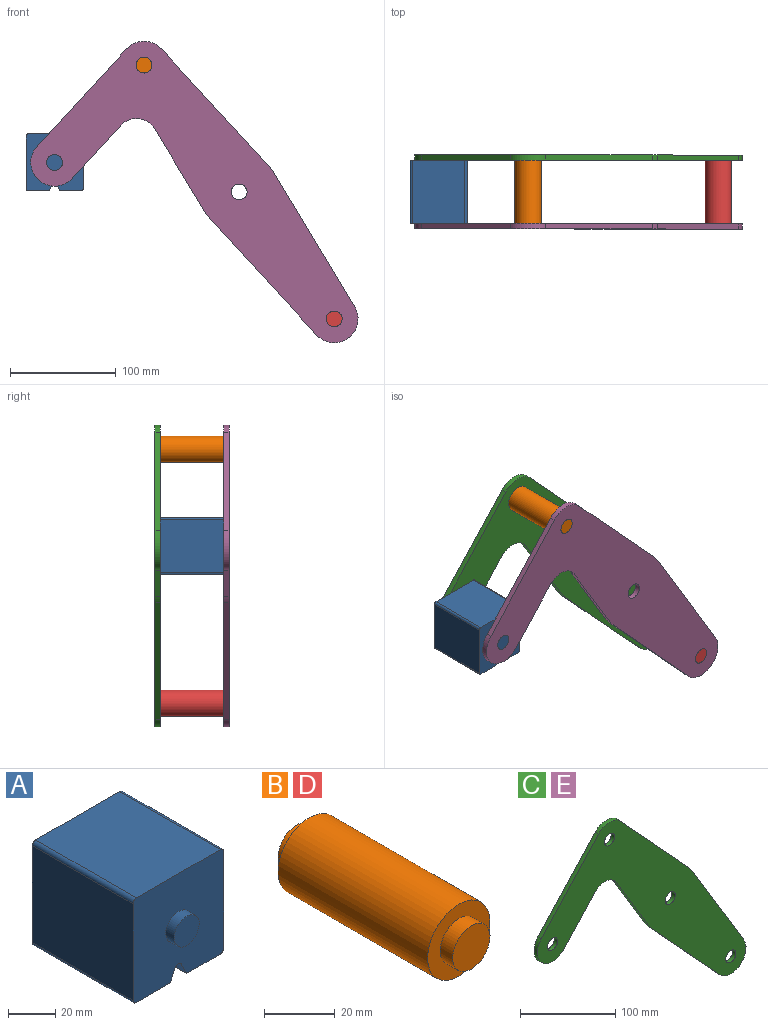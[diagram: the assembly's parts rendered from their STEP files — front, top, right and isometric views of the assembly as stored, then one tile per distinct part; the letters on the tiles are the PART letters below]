
ASSEMBLY  parts=5 mates=3
PART A: 18 faces, bbox 54x70x54 mm
  f0: plane 60x50.01mm, normal (0,0,1), area 3000.4mm2, adj f4,f10,f13,f14
  f1: plane 60x50.01mm, normal (-1,0,0), area 3000.4mm2, adj f4,f10,f14,f15
  f2: plane 60x20mm, normal (0,0,-1), area 1200.2mm2, adj f3,f4,f10,f15
  f3: plane 60x6.42mm, normal (0.89,0,-0.45), area 430.8mm2, adj f2,f4,f10,f16
  f4: plane 54.01x54.01mm, normal (0,-1,0), area 2690.1mm2, adj f0,f1,f2,f3,f5,f6,f7,f9
  f5: plane 60x50.01mm, normal (1,0,0), area 3000.4mm2, adj f4,f10,f13,f17
  f6: plane 60x6.42mm, normal (-0.89,0,-0.45), area 430.8mm2, adj f4,f7,f10,f16
  f7: plane 60x20mm, normal (0,0,-1), area 1200.2mm2, adj f4,f6,f10,f17
  f8: plane 15x15mm, normal (0,-1,0), area 176.7mm2, adj f9
  f9: cylinder r=7.5mm len=15mm, axis (0,1,0), area 235.6mm2, adj f4,f8
  f10: plane 54.01x54.01mm, normal (0,1,0), area 2690.1mm2, adj f0,f1,f2,f3,f5,f6,f7,f12
  f11: plane 15x15mm, normal (0,1,0), area 176.7mm2, adj f12
  f12: cylinder r=7.5mm len=15mm, axis (0,-1,0), area 235.6mm2, adj f10,f11
  f13: cylinder r=2mm len=60mm, axis (0,-1,0), area 188.5mm2, adj f0,f4,f5,f10
  f14: cylinder r=2mm len=60mm, axis (0,1,0), area 188.5mm2, adj f0,f1,f4,f10
  f15: cylinder r=2mm len=60mm, axis (0,-1,0), area 188.5mm2, adj f1,f2,f4,f10
  f16: cylinder r=2mm len=60mm, axis (0,-1,0), area 265.7mm2, adj f3,f4,f6,f10
  f17: cylinder r=2mm len=60mm, axis (0,1,0), area 188.5mm2, adj f4,f5,f7,f10
PART B: 7 faces, bbox 25x70x25 mm
  f0: cylinder r=12.5mm len=60mm, axis (0,-1,0), area 4712.4mm2, adj f2,f5
  f1: cylinder r=7.5mm len=15mm, axis (0,1,0), area 235.6mm2, adj f2,f3
  f2: plane 25x25mm, normal (0,-1,0), area 314.2mm2, adj f0,f1
  f3: plane 15x15mm, normal (0,-1,0), area 176.7mm2, adj f1
  f4: cylinder r=7.5mm len=15mm, axis (0,-1,0), area 235.6mm2, adj f5,f6
  f5: plane 25x25mm, normal (0,1,0), area 314.2mm2, adj f0,f4
  f6: plane 15x15mm, normal (0,1,0), area 176.7mm2, adj f4
PART C: 18 faces, bbox 309.5x5x285.1 mm
  f0: cylinder r=22.5mm len=39.07mm, axis (0,1,0), area 353.4mm2, adj f1,f13,f16,f17
  f1: plane 50.28x46.21mm, normal (0.74,0,-0.68), area 341.4mm2, adj f0,f2,f16,f17
  f2: cylinder r=20mm len=31.85mm, axis (0,1,0), area 185.5mm2, adj f1,f3,f16,f17
  f3: plane 79.23x47.81mm, normal (-0.86,0,-0.52), area 462.7mm2, adj f2,f4,f16,f17
  f4: cylinder r=37.5mm len=6mm, axis (0,1,0), area 37.6mm2, adj f3,f5,f16,f17
  f5: plane 109.88x101mm, normal (-0.74,0,-0.68), area 746.2mm2, adj f4,f6,f16,f17
  f6: cylinder r=22.5mm len=39.07mm, axis (0,1,0), area 330.9mm2, adj f5,f7,f16,f17
  f7: plane 127.78x77.11mm, normal (0.86,0,0.52), area 746.2mm2, adj f6,f8,f16,f17
  f8: cylinder r=37.5mm len=6mm, axis (0,1,0), area 37.6mm2, adj f7,f9,f16,f17
  f9: plane 109.88x101mm, normal (0.74,0,0.68), area 746.2mm2, adj f8,f10,f16,f17
  f10: cylinder r=22.5mm len=33.13mm, axis (0,1,0), area 186.2mm2, adj f9,f13,f16,f17
  f11: cylinder r=7.5mm len=15mm, axis (0,1,0), area 235.6mm2, adj f16,f17
  f12: cylinder r=7.5mm len=15mm, axis (0,1,0), area 235.6mm2, adj f16,f17
  f13: plane 92.03x84.59mm, normal (-0.74,0,0.68), area 625mm2, adj f0,f10,f16,f17
  f14: cylinder r=7.5mm len=15mm, axis (0,1,0), area 235.6mm2, adj f16,f17
  f15: cylinder r=7.5mm len=15mm, axis (0,1,0), area 235.6mm2, adj f16,f17
  f16: plane 309.5x285.07mm, normal (0,-1,0), area 24555.4mm2, adj f0,f1,f2,f3,f4,f5,f6,f7
  f17: plane 309.5x285.07mm, normal (0,1,0), area 24555.4mm2, adj f0,f1,f2,f3,f4,f5,f6,f7
PART D: same geometry as B
PART E: same geometry as C
PLACE A t=(0,-30,0)mm
PLACE B t=(0,-30,0)mm
PLACE C t=(0,35,0)mm
PLACE D t=(179.91,-30,-240.07)mm
PLACE E t=(0,-30,0)mm fixed
MATE fastened D.f0 <-> E.f6  axis (0,-1,0) through (89.96,-30,-120.03)mm
MATE fastened C.f10 <-> B.f0  axis (0,-1,0) through (-89.96,30,120.03)mm
MATE revolute E.f0 <-> A.f9  axis (0,1,0) through (-174.54,-30,28)mm
